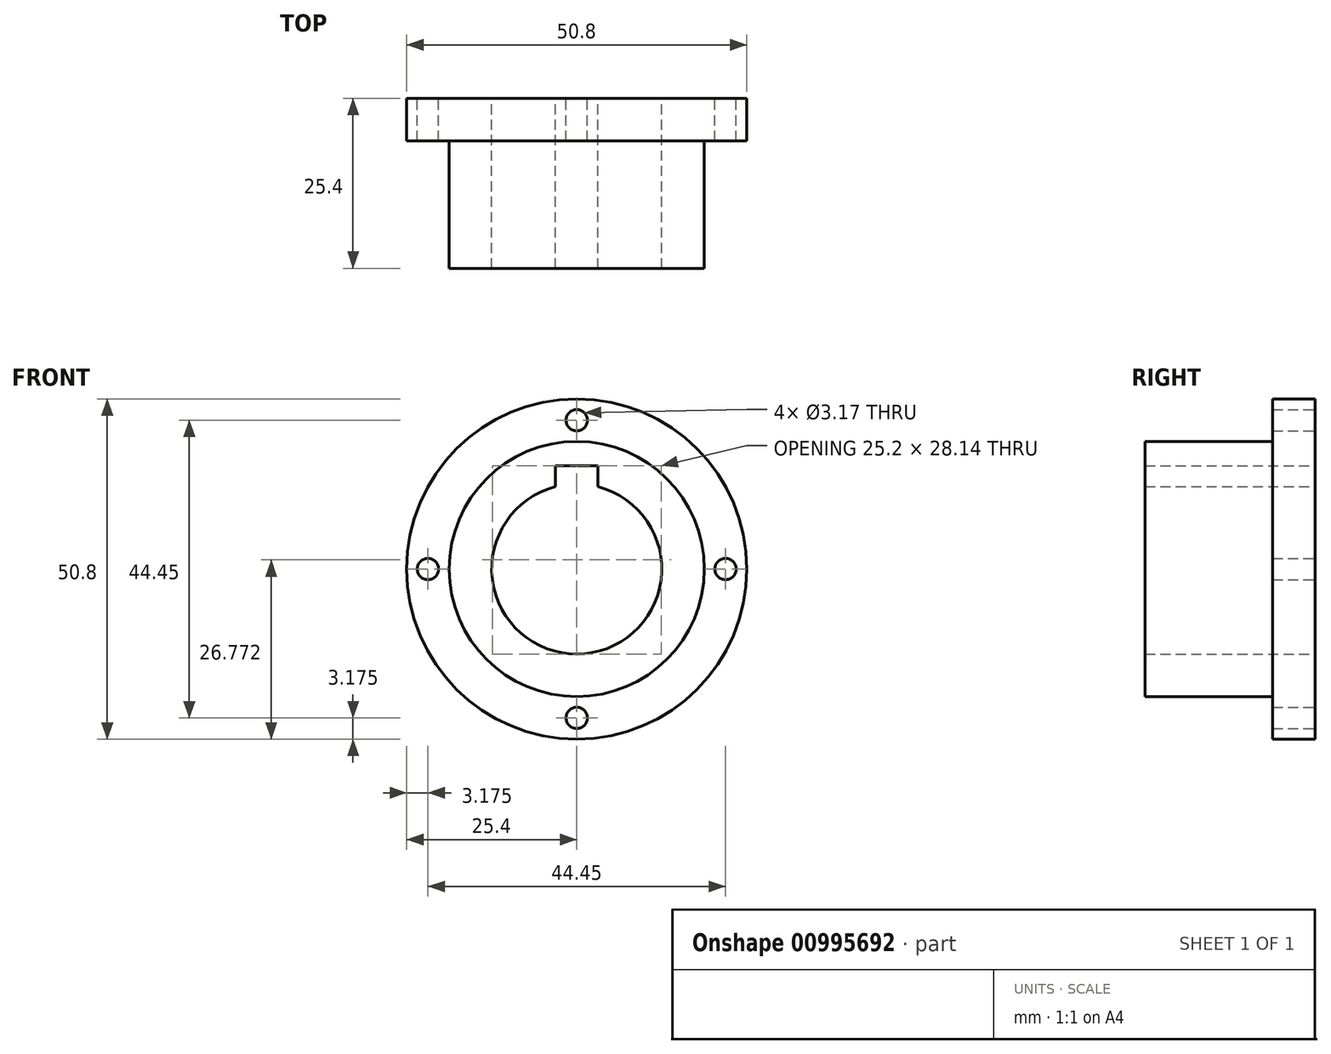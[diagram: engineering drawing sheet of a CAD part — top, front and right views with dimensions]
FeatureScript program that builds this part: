
annotation { "Feature Type Name" : "Feature", "Feature Type Description" : "" }
export const myFeature = defineFeature(function(context is Context, id is Id, definition is map)
    precondition{}
    {
        {
            var Q0;
            Q0=qCreatedBy(makeId("Front.planeOp"),FACE);
            var sketch = newSketch(context, id + "F0", { "sketchPlane" : qUnion([Q0])});
            skCircle(sketch, "E0", {"center": v(0, 0) * mm, "radius": 12.7 * mm});
            skCircle(sketch, "E1", {"center": v(0, 22.23) * mm, "radius": 1.59 * mm});
            skCircle(sketch, "E2", {"center": v(0, 0) * mm, "radius": 22.23 * mm, "construction": true});
            skCircle(sketch, "E3.1.0", {"center": v(-22.23, 0) * mm, "radius": 1.59 * mm});
            skCircle(sketch, "E3.2.0", {"center": v(0, -22.23) * mm, "radius": 1.59 * mm});
            skCircle(sketch, "E3.3.0", {"center": v(22.23, 0) * mm, "radius": 1.59 * mm});
            skCircle(sketch, "E4", {"center": v(0, 0) * mm, "radius": 25.4 * mm});
            skSolve(sketch);
        }
        {
            var Q0;
            Q0=qSketchRegion(id+"F0",true);
            extrude(context, id + "F1", {"entities" : qUnion([Q0]), "depth" : 6.35 * mm, "offsetDistance" : 25.4 * mm});
        }
        {
            var Q0;
            Q0=qCreatedBy(makeId("Front.planeOp"),FACE);
            var sketch = newSketch(context, id + "F2", { "sketchPlane" : qUnion([Q0])});
            skCircle(sketch, "E5", {"center": v(0, 0) * mm, "radius": 19.05 * mm});
            skCircle(sketch, "E6.0", {"center": v(0, 0) * mm, "radius": 12.7 * mm});
            skSolve(sketch);
        }
        {
            var Q0;
            Q0=makeQuery(id+"F2.imprint","IMPRINT",FACE,{"disambiguationData":[TD([[makeQuery(id+"F2.imprint","IMPRINT",EDGE,{"derivedFrom":sQuery(id+"F2.wireOp",EDGE,"E5")}),1.0]])]});
            extrude(context, id + "F3", {"entities" : qUnion([Q0]), "operationType" : NewBodyOperationType.ADD, "depth" : 25.4 * mm, "offsetDistance" : 25.4 * mm});
        }
        {
            var Q0;
            Q0=qCreatedBy(makeId("Front.planeOp"),FACE);
            var sketch = newSketch(context, id + "F4", { "sketchPlane" : qUnion([Q0])});
            skLineSegment(sketch, "E7.bottom", {"start": v(-3.18, 0) * mm, "end": v(3.18, 0) * mm});
            skLineSegment(sketch, "E7.top", {"start": v(-3.18, 15.44) * mm, "end": v(3.17, 15.44) * mm});
            skLineSegment(sketch, "E7.left", {"start": v(-3.18, 0) * mm, "end": v(-3.17, 15.44) * mm});
            skLineSegment(sketch, "E7.right", {"start": v(3.17, 0) * mm, "end": v(3.18, 15.44) * mm});
            skPoint(sketch, "E8", {"position": v(0, 12.7) * mm});
            skLineSegment(sketch, "E9", {"start": v(0, 12.7) * mm, "end": v(0, 15.44) * mm, "construction": true});
            skSolve(sketch);
        }
        {
            var Q0;
            Q0=makeQuery(id+"F4.imprint","IMPRINT",FACE,{"disambiguationData":[TD([[makeQuery(id+"F4.imprint","IMPRINT",EDGE,{"derivedFrom":sQuery(id+"F4.wireOp",EDGE,"E7.bottom")}),1.0]])]});
            extrude(context, id + "F5", {"entities" : qUnion([Q0]), "operationType" : NewBodyOperationType.REMOVE, "endBound" : BoundingType.THROUGH_ALL, "depth" : 25.4 * mm, "offsetDistance" : 25.4 * mm});
        }
    });
